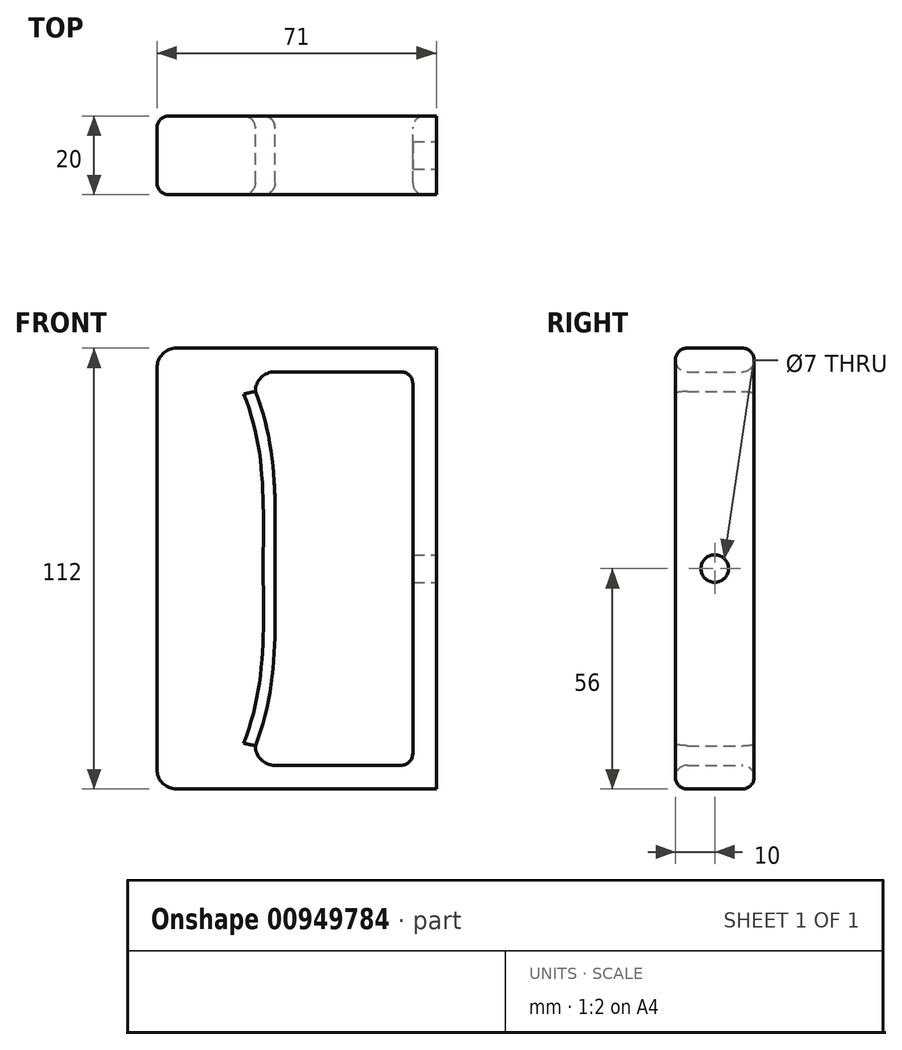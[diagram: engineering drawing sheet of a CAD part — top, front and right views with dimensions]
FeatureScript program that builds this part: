
annotation { "Feature Type Name" : "Feature", "Feature Type Description" : "" }
export const myFeature = defineFeature(function(context is Context, id is Id, definition is map)
    precondition{}
    {
        {
            var Q0;
            Q0=qCreatedBy(makeId("Front.planeOp"),FACE);
            var sketch = newSketch(context, id + "F0", { "sketchPlane" : qUnion([Q0])});
            skLineSegment(sketch, "E0.bottom", {"start": v(0, 112) * mm, "end": v(-6, 112) * mm});
            skLineSegment(sketch, "E0.top", {"start": v(0, 0) * mm, "end": v(-6, 0) * mm});
            skLineSegment(sketch, "E0.left", {"start": v(0, 112) * mm, "end": v(0, 0) * mm});
            skLineSegment(sketch, "E0.right", {"start": v(-6, 112) * mm, "end": v(-6, 0) * mm});
            skLineSegment(sketch, "E1.bottom", {"start": v(0, 112) * mm, "end": v(-71, 112) * mm});
            skLineSegment(sketch, "E1.top", {"start": v(0, 0) * mm, "end": v(-71, 0) * mm});
            skLineSegment(sketch, "E1.right", {"start": v(-71, 112) * mm, "end": v(-71, 0) * mm});
            skLineSegment(sketch, "E2.bottom", {"start": v(-6, 106) * mm, "end": v(-46, 106) * mm});
            skLineSegment(sketch, "E2.top", {"start": v(-6, 6) * mm, "end": v(-46, 6) * mm});
            skLineSegment(sketch, "E2.left", {"start": v(-6, 106) * mm, "end": v(-6, 6) * mm});
            skLineSegment(sketch, "E2.right", {"start": v(-46, 106) * mm, "end": v(-46, 6) * mm});
            skSolve(sketch);
        }
        {
            var Q0;
            {var subQ4=sQuery(id+"F0.wireOp",EDGE,"E0.bottom");Q0=makeQuery(id+"F0.imprint","IMPRINT",FACE,{"disambiguationData":[TD([[makeQuery(id+"F0.imprint","IMPRINT",EDGE,{"derivedFrom":subQ4}),1.0]])]});}
            var Q1;
            {var subQ1=sQuery(id+"F0.wireOp",EDGE,"E1.bottom");Q1=makeQuery(id+"F0.imprint","IMPRINT",FACE,{"disambiguationData":[TD([[makeQuery(id+"F0.imprint","IMPRINT",EDGE,{"derivedFrom":subQ1}),1.0]])]});}
            extrude(context, id + "F1", {"entities" : qUnion([Q0, Q1]), "depth" : 20 * mm, "offsetDistance" : 25 * mm});
        }
        {
            var Q0;
            Q0=makeQuery(id+"F1.opExtrude","SWEPT_EDGE",EDGE,{"disambiguationData":[OSD([sQuery(id+"F0.wireOp",EDGE,"E1.bottom"),sQuery(id+"F0.wireOp",EDGE,"E1.right")])]});
            var Q1;
            Q1=makeQuery(id+"F1.opExtrude","SWEPT_EDGE",EDGE,{"disambiguationData":[OSD([sQuery(id+"F0.wireOp",EDGE,"E1.top"),sQuery(id+"F0.wireOp",EDGE,"E1.right")])]});
            var Q2;
            Q2=makeQuery(id+"F1.opExtrude","SWEPT_EDGE",EDGE,{"disambiguationData":[OSD([sQuery(id+"F0.wireOp",EDGE,"E2.bottom"),sQuery(id+"F0.wireOp",EDGE,"E2.right")])]});
            var Q3;
            Q3=makeQuery(id+"F1.opExtrude","SWEPT_EDGE",EDGE,{"disambiguationData":[OSD([sQuery(id+"F0.wireOp",EDGE,"E2.top"),sQuery(id+"F0.wireOp",EDGE,"E2.right")])]});
            fillet(context, id + "F2", {"entities" : qUnion([Q0, Q1, Q2, Q3]), "radius" : 5 * mm, "tangentPropagation" : true, "allowEdgeOverflow" : false});
        }
        {
            var Q0;
            Q0=makeQuery(id+"F1.opExtrude","SWEPT_FACE",FACE,{"disambiguationData":[OSD([sQuery(id+"F0.wireOp",EDGE,"E0.left")])]});
            var sketch = newSketch(context, id + "F3", { "sketchPlane" : qUnion([Q0])});
            skCircle(sketch, "E3", {"center": v(-10, 56) * mm, "radius": 3.5 * mm});
            skLineSegment(sketch, "E4", {"start": v(-10, 112) * mm, "end": v(-10, 56) * mm, "construction": true});
            skLineSegment(sketch, "E5", {"start": v(-10, 56) * mm, "end": v(-10, 0) * mm, "construction": true});
            skLineSegment(sketch, "E6", {"start": v(-20, 56) * mm, "end": v(-10, 56) * mm, "construction": true});
            skLineSegment(sketch, "E7", {"start": v(-10, 56) * mm, "end": v(0, 56) * mm, "construction": true});
            skPoint(sketch, "E7.endSnap0", {"position": v(0, 56) * mm});
            skSolve(sketch);
        }
        {
            var Q0;
            Q0=makeQuery(id+"F3.imprint","IMPRINT",FACE,{"disambiguationData":[TD([[makeQuery(id+"F3.imprint","IMPRINT",EDGE,{"derivedFrom":sQuery(id+"F3.wireOp",EDGE,"E3")}),1.0]])]});
            extrude(context, id + "F4", {"entities" : qUnion([Q0]), "operationType" : NewBodyOperationType.REMOVE, "oppositeDirection" : true, "depth" : 25 * mm, "offsetDistance" : 25 * mm});
        }
        {
            var Q0;
            Q0=makeQuery(id+"F1.opExtrude","CAP_FACE",FACE,{"disambiguationData":[OSD([sQuery(id+"F0.wireOp",EDGE,"E0.bottom"),sQuery(id+"F0.wireOp",EDGE,"E0.top"),sQuery(id+"F0.wireOp",EDGE,"E0.left"),sQuery(id+"F0.wireOp",EDGE,"E0.right"),sQuery(id+"F0.wireOp",EDGE,"E1.bottom"),sQuery(id+"F0.wireOp",EDGE,"E1.top"),sQuery(id+"F0.wireOp",EDGE,"E1.right"),sQuery(id+"F0.wireOp",EDGE,"E2.bottom"),sQuery(id+"F0.wireOp",EDGE,"E2.top"),sQuery(id+"F0.wireOp",EDGE,"E2.right")])],"isStart":false});
            var sketch = newSketch(context, id + "F5", { "sketchPlane" : qUnion([Q0])});
            skFitSpline(sketch, "E8", {"points": [v(-46, 101) * mm, v(-41, 56.65) * mm, v(-46, 11) * mm], "startDerivative": vector(35.79, -88.97) * mm, "endDerivative": vector(-35.63, -91.03) * mm});
            skLineSegment(sketch, "E9", {"start": v(-41, 56.65) * mm, "end": v(-46, 56.65) * mm});
            skSolve(sketch);
        }
        {
            var Q0;
            Q0 = qSketchRegion(id + "F5", true);
            var Q1;
            {var subQ5=sQuery(id+"F5.wireOp",EDGE,"E9");Q1=makeQuery(id+"F5.imprint","IMPRINT",FACE,{"disambiguationData":[TD([[makeQuery(id+"F5.imprint","IMPRINT",EDGE,{"derivedFrom":subQ5}),-1.0]])]});}
            var Q2;
            {var subQ5=sQuery(id+"F5.wireOp",EDGE,"E9");Q2=makeQuery(id+"F5.imprint","IMPRINT",FACE,{"disambiguationData":[TD([[makeQuery(id+"F5.imprint","IMPRINT",EDGE,{"derivedFrom":subQ5}),1.0]])]});}
            var Q3;
            Q3=makeQuery(id+"F1.opExtrude","CAP_FACE",FACE,{"disambiguationData":[OSD([sQuery(id+"F0.wireOp",EDGE,"E0.bottom"),sQuery(id+"F0.wireOp",EDGE,"E0.top"),sQuery(id+"F0.wireOp",EDGE,"E0.left"),sQuery(id+"F0.wireOp",EDGE,"E0.right"),sQuery(id+"F0.wireOp",EDGE,"E1.bottom"),sQuery(id+"F0.wireOp",EDGE,"E1.top"),sQuery(id+"F0.wireOp",EDGE,"E1.right"),sQuery(id+"F0.wireOp",EDGE,"E2.bottom"),sQuery(id+"F0.wireOp",EDGE,"E2.top"),sQuery(id+"F0.wireOp",EDGE,"E2.right")])],"isStart":true});
            extrude(context, id + "F6", {"entities" : qUnion([Q0, Q1, Q2]), "operationType" : NewBodyOperationType.ADD, "endBound" : BoundingType.UP_TO_SURFACE, "oppositeDirection" : true, "depth" : 25 * mm, "endBoundEntityFace" : qUnion([Q3]), "offsetDistance" : 25 * mm});
        }
        {
            var Q0;
            Q0=makeQuery(id+"F1.opExtrude","SWEPT_EDGE",EDGE,{"disambiguationData":[OSD([sQuery(id+"F0.wireOp",EDGE,"E0.right"),sQuery(id+"F0.wireOp",EDGE,"E2.bottom")])]});
            var Q1;
            Q1=makeQuery(id+"F1.opExtrude","SWEPT_EDGE",EDGE,{"disambiguationData":[OSD([sQuery(id+"F0.wireOp",EDGE,"E0.right"),sQuery(id+"F0.wireOp",EDGE,"E2.top")])]});
            fillet(context, id + "F7", {"entities" : qUnion([Q0, Q1]), "radius" : 3 * mm, "tangentPropagation" : true, "allowEdgeOverflow" : false});
        }
        {
            var Q0;
            Q0=makeQuery(id+"F6.opExtrude","CAP_EDGE",EDGE,{"disambiguationData":[OSD([sQuery(id+"F5.wireOp",EDGE,"E8")])],"isStart":true});
            var Q1;
            {var subQ0=sQuery(id+"F0.wireOp",EDGE,"E2.right");var subQ1=sQuery(id+"F0.wireOp",EDGE,"E2.bottom");Q1=makeQuery(id+"F2.opFillet","BLEND_EDGE",EDGE,{"blendedFrom":[makeQuery(id+"F1.opExtrude","SWEPT_EDGE",EDGE,{"disambiguationData":[OSD([subQ1,subQ0])]}),makeQuery(id+"F1.opExtrude","CAP_FACE",FACE,{"disambiguationData":[OSD([sQuery(id+"F0.wireOp",EDGE,"E0.bottom"),sQuery(id+"F0.wireOp",EDGE,"E0.top"),sQuery(id+"F0.wireOp",EDGE,"E0.left"),sQuery(id+"F0.wireOp",EDGE,"E0.right"),sQuery(id+"F0.wireOp",EDGE,"E1.bottom"),sQuery(id+"F0.wireOp",EDGE,"E1.top"),sQuery(id+"F0.wireOp",EDGE,"E1.right"),subQ1,sQuery(id+"F0.wireOp",EDGE,"E2.top"),subQ0])],"isStart":false})],"blendedInto":[makeQuery(id+"F1.opExtrude","CAP_FACE",FACE,{"disambiguationData":[OSD([sQuery(id+"F0.wireOp",EDGE,"E0.bottom"),sQuery(id+"F0.wireOp",EDGE,"E0.top"),sQuery(id+"F0.wireOp",EDGE,"E0.left"),sQuery(id+"F0.wireOp",EDGE,"E0.right"),sQuery(id+"F0.wireOp",EDGE,"E1.bottom"),sQuery(id+"F0.wireOp",EDGE,"E1.top"),sQuery(id+"F0.wireOp",EDGE,"E1.right"),subQ1,sQuery(id+"F0.wireOp",EDGE,"E2.top"),subQ0])],"isStart":false})]});}
            var Q2;
            Q2=makeQuery(id+"F1.opExtrude","CAP_EDGE",EDGE,{"disambiguationData":[OSD([sQuery(id+"F0.wireOp",EDGE,"E2.bottom")])],"isStart":false});
            fillet(context, id + "F8", {"entities" : qUnion([Q0, Q1, Q2]), "radius" : 3 * mm, "tangentPropagation" : true, "allowEdgeOverflow" : false});
        }
        {
            var Q0;
            Q0=makeQuery(id+"F1.opExtrude","CAP_EDGE",EDGE,{"disambiguationData":[OSD([sQuery(id+"F0.wireOp",EDGE,"E2.top")])],"isStart":true});
            var Q1;
            Q1=makeQuery(id+"F6.opExtrude","CAP_EDGE",EDGE,{"disambiguationData":[OSD([sQuery(id+"F5.wireOp",EDGE,"E8")])],"isStart":false});
            fillet(context, id + "F9", {"entities" : qUnion([Q0, Q1]), "radius" : 3 * mm, "tangentPropagation" : true, "allowEdgeOverflow" : false});
        }
        {
            var Q0;
            Q0=makeQuery(id+"F1.opExtrude","CAP_EDGE",EDGE,{"disambiguationData":[OSD([sQuery(id+"F0.wireOp",EDGE,"E1.right")])],"isStart":false});
            var Q1;
            Q1=makeQuery(id+"F1.opExtrude","CAP_EDGE",EDGE,{"disambiguationData":[OSD([sQuery(id+"F0.wireOp",EDGE,"E0.bottom"),sQuery(id+"F0.wireOp",EDGE,"E1.bottom")])],"isStart":true});
            fillet(context, id + "F10", {"entities" : qUnion([Q0, Q1]), "radius" : 3 * mm, "tangentPropagation" : true, "allowEdgeOverflow" : false});
        }
    });
